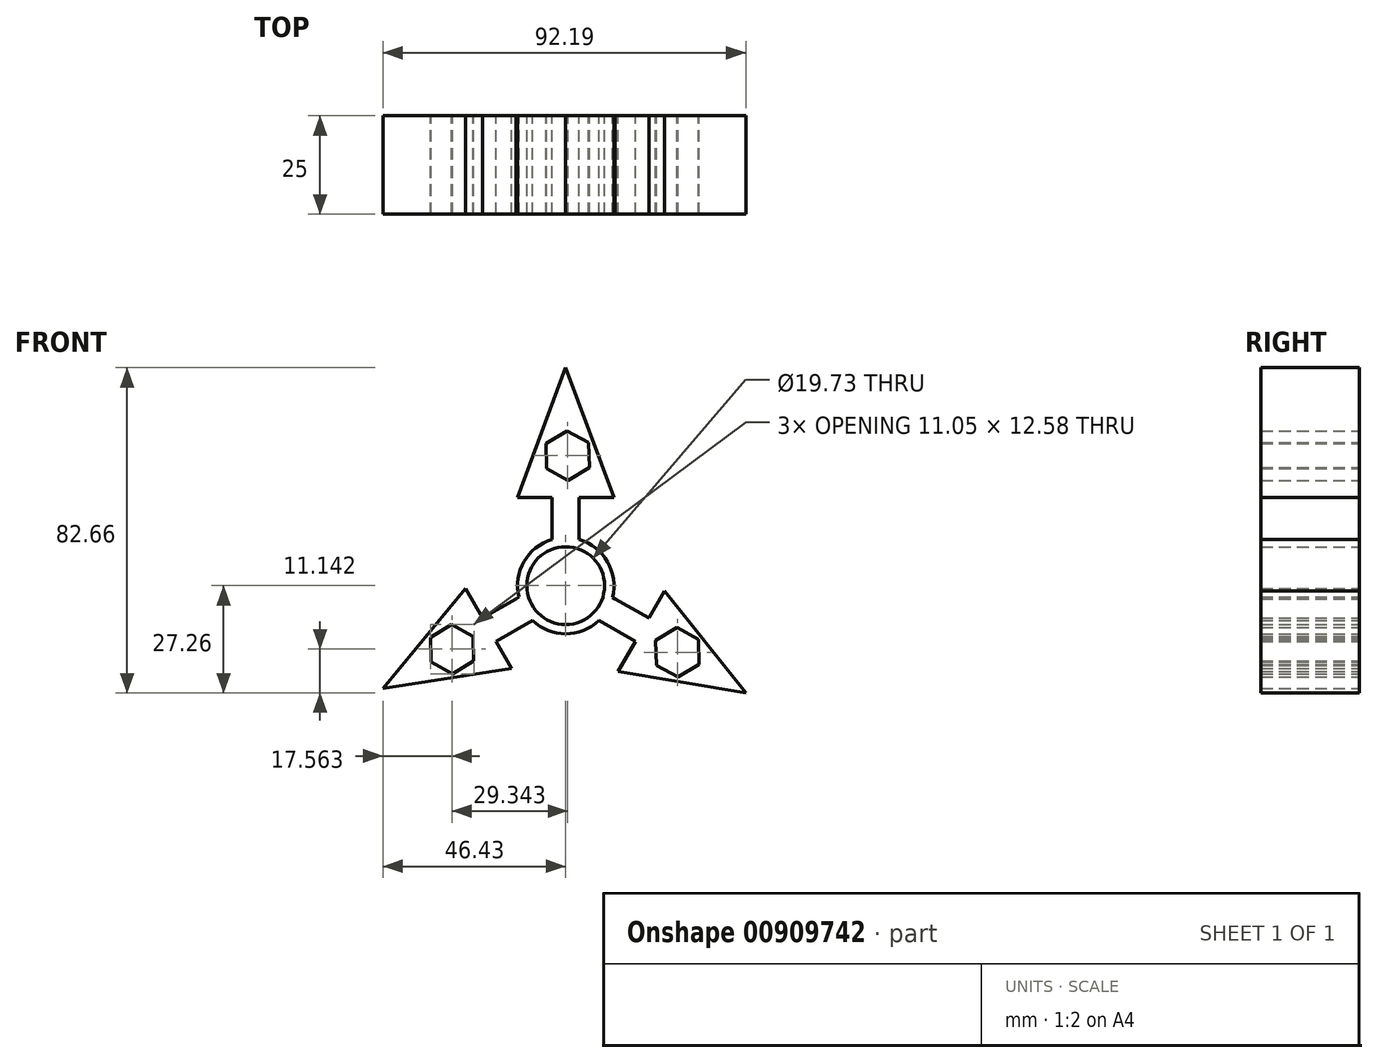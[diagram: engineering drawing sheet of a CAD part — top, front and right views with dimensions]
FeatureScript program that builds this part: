
annotation { "Feature Type Name" : "Feature", "Feature Type Description" : "" }
export const myFeature = defineFeature(function(context is Context, id is Id, definition is map)
    precondition{}
    {
        {
            var Q0;
            Q0=qCreatedBy(makeId("Front.planeOp"),FACE);
            var sketch = newSketch(context, id + "F0", { "sketchPlane" : qUnion([Q0])});
            skCircle(sketch, "E0", {"center": v(0, 0) * mm, "radius": 12.23 * mm});
            skLineSegment(sketch, "E1", {"start": v(-3.43, 12.56) * mm, "end": v(-3.43, 22.4) * mm});
            skLineSegment(sketch, "E2", {"start": v(-3.43, 22.4) * mm, "end": v(-12.23, 22.4) * mm});
            skLineSegment(sketch, "E3", {"start": v(-12.23, 22.4) * mm, "end": v(0, 55.4) * mm});
            skLineSegment(sketch, "E4.MirrorCS", {"start": v(3.43, 12.56) * mm, "end": v(3.43, 22.4) * mm});
            skLineSegment(sketch, "E5.MirrorCS", {"start": v(3.43, 22.4) * mm, "end": v(12.23, 22.4) * mm});
            skLineSegment(sketch, "E6.MirrorCS", {"start": v(12.23, 22.4) * mm, "end": v(0, 55.4) * mm});
            skPoint(sketch, "E7.0.midPoint", {"position": v(-3.43, 22.4) * mm});
            skPoint(sketch, "E8", {"position": v(0, 55.4) * mm});
            skLineSegment(sketch, "E9.1.0", {"start": v(-13.74, -21.02) * mm, "end": v(-46.43, -26.04) * mm});
            skLineSegment(sketch, "E9.1.1", {"start": v(-25.45, -0.74) * mm, "end": v(-46.43, -26.04) * mm});
            skLineSegment(sketch, "E9.1.2", {"start": v(-17.7, -14.17) * mm, "end": v(-13.74, -21.02) * mm});
            skLineSegment(sketch, "E9.1.3", {"start": v(-9.17, -9.25) * mm, "end": v(-17.7, -14.17) * mm});
            skLineSegment(sketch, "E9.1.4", {"start": v(-12.6, -3.31) * mm, "end": v(-21.12, -8.24) * mm});
            skLineSegment(sketch, "E9.2.0", {"start": v(25.07, -1.39) * mm, "end": v(45.76, -27.26) * mm});
            skLineSegment(sketch, "E9.2.1", {"start": v(13.32, -21.74) * mm, "end": v(45.76, -27.26) * mm});
            skLineSegment(sketch, "E9.2.2", {"start": v(21.12, -8.24) * mm, "end": v(25.07, -1.39) * mm});
            skLineSegment(sketch, "E9.2.3", {"start": v(12.6, -3.31) * mm, "end": v(21.12, -8.24) * mm});
            skLineSegment(sketch, "E9.2.4", {"start": v(9.17, -9.25) * mm, "end": v(17.7, -14.17) * mm});
            skLineSegment(sketch, "E10", {"start": v(-25.45, -0.74) * mm, "end": v(-21.12, -8.24) * mm});
            skLineSegment(sketch, "E11", {"start": v(17.7, -14.17) * mm, "end": v(13.32, -21.74) * mm});
            skLineSegment(sketch, "E12", {"start": v(-3.43, 12.56) * mm, "end": v(-3.43, 11.74) * mm});
            skLineSegment(sketch, "E13", {"start": v(3.43, 12.56) * mm, "end": v(3.43, 11.74) * mm});
            skLineSegment(sketch, "E14", {"start": v(-9.17, -9.25) * mm, "end": v(-8.45, -8.84) * mm});
            skLineSegment(sketch, "E15", {"start": v(-12.6, -3.31) * mm, "end": v(-11.88, -2.92) * mm});
            skLineSegment(sketch, "E16", {"start": v(9.17, -9.25) * mm, "end": v(8.45, -8.84) * mm});
            skLineSegment(sketch, "E17", {"start": v(12.6, -3.31) * mm, "end": v(11.85, -3.03) * mm});
            skCircle(sketch, "E18.cCircle", {"center": v(0.48, 33.06) * mm, "radius": 5.45 * mm, "construction": true});
            skLineSegment(sketch, "E18.0", {"start": v(0.63, 26.77) * mm, "end": v(-4.9, 29.78) * mm});
            skLineSegment(sketch, "E18.1", {"start": v(-4.9, 29.78) * mm, "end": v(-5.05, 36.07) * mm});
            skLineSegment(sketch, "E18.2", {"start": v(-5.05, 36.07) * mm, "end": v(0.32, 39.35) * mm});
            skLineSegment(sketch, "E18.3", {"start": v(0.32, 39.35) * mm, "end": v(5.85, 36.34) * mm});
            skLineSegment(sketch, "E18.4", {"start": v(5.85, 36.34) * mm, "end": v(6, 30.05) * mm});
            skLineSegment(sketch, "E18.5", {"start": v(6, 30.05) * mm, "end": v(0.63, 26.77) * mm});
            skPoint(sketch, "E18.0.midPoint", {"position": v(-2.13, 28.27) * mm});
            skLineSegment(sketch, "E19.1.0", {"start": v(-28.71, -22.4) * mm, "end": v(-34.24, -19.4) * mm});
            skLineSegment(sketch, "E19.1.1", {"start": v(-34.24, -19.4) * mm, "end": v(-34.4, -13.1) * mm});
            skLineSegment(sketch, "E19.1.2", {"start": v(-34.4, -13.1) * mm, "end": v(-29.02, -9.83) * mm});
            skLineSegment(sketch, "E19.1.3", {"start": v(-29.02, -9.83) * mm, "end": v(-23.5, -12.84) * mm});
            skLineSegment(sketch, "E19.1.4", {"start": v(-23.5, -12.84) * mm, "end": v(-23.34, -19.13) * mm});
            skLineSegment(sketch, "E19.1.5", {"start": v(-23.34, -19.13) * mm, "end": v(-28.71, -22.4) * mm});
            skCircle(sketch, "E19.1.6", {"center": v(-28.87, -16.12) * mm, "radius": 5.45 * mm, "construction": true});
            skLineSegment(sketch, "E19.2.0", {"start": v(33.76, -13.66) * mm, "end": v(33.92, -19.95) * mm});
            skLineSegment(sketch, "E19.2.1", {"start": v(33.92, -19.95) * mm, "end": v(28.54, -23.23) * mm});
            skLineSegment(sketch, "E19.2.2", {"start": v(28.54, -23.23) * mm, "end": v(23.02, -20.22) * mm});
            skLineSegment(sketch, "E19.2.3", {"start": v(23.02, -20.22) * mm, "end": v(22.87, -13.93) * mm});
            skLineSegment(sketch, "E19.2.4", {"start": v(22.87, -13.93) * mm, "end": v(28.24, -10.65) * mm});
            skLineSegment(sketch, "E19.2.5", {"start": v(28.24, -10.65) * mm, "end": v(33.76, -13.66) * mm});
            skCircle(sketch, "E19.2.6", {"center": v(28.4, -16.94) * mm, "radius": 5.45 * mm, "construction": true});
            skCircle(sketch, "E20", {"center": v(0, 0) * mm, "radius": 9.87 * mm});
            skSolve(sketch);
        }
        {
            var Q0;
            Q0=makeQuery(id+"F0.imprint","IMPRINT",FACE,{"disambiguationData":[TD([[makeQuery(id+"F0.imprint","IMPRINT",EDGE,{"derivedFrom":sQuery(id+"F0.wireOp",EDGE,"E1")}),-1.0]])]});
            var Q1;
            Q1=makeQuery(id+"F0.imprint","IMPRINT",FACE,{"disambiguationData":[TD([[makeQuery(id+"F0.imprint","IMPRINT",EDGE,{"derivedFrom":sQuery(id+"F0.wireOp",EDGE,"E9.1.0")}),-1.0]])]});
            var Q2;
            Q2=makeQuery(id+"F0.imprint","IMPRINT",FACE,{"disambiguationData":[TD([[makeQuery(id+"F0.imprint","IMPRINT",EDGE,{"derivedFrom":sQuery(id+"F0.wireOp",EDGE,"E9.2.0")}),-1.0]])]});
            var Q3;
            Q3=makeQuery(id+"F0.imprint","IMPRINT",FACE,{"disambiguationData":[TD([[makeQuery(id+"F0.imprint","IMPRINT",EDGE,{"derivedFrom":sQuery(id+"F0.wireOp",EDGE,"E20")}),-1.0]])]});
            extrude(context, id + "F1", {"entities" : qUnion([Q0, Q1, Q2, Q3]), "depth" : 25 * mm, "offsetDistance" : 25 * mm});
        }
    });
